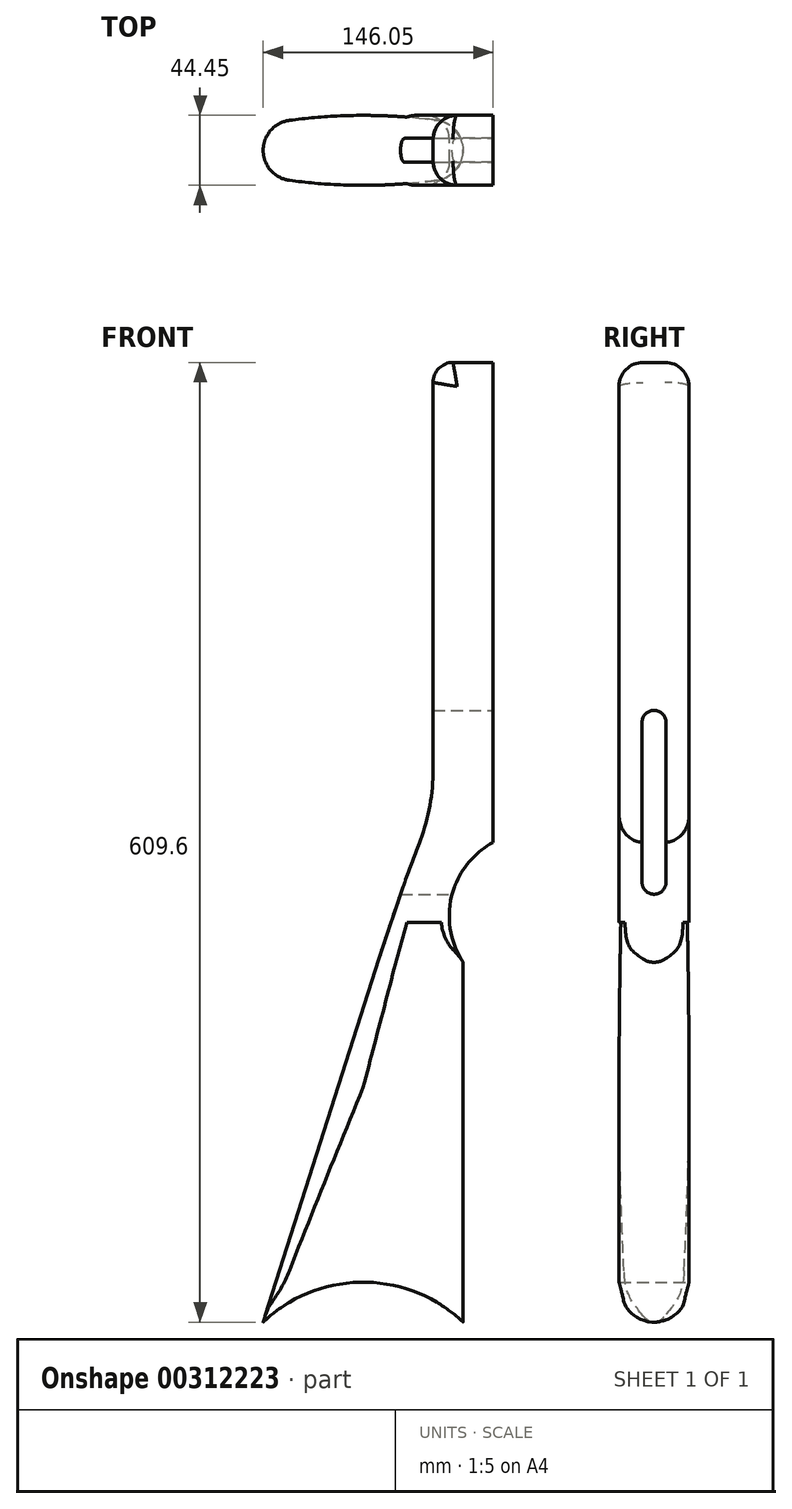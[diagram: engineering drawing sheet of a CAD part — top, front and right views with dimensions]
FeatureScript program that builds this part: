
annotation { "Feature Type Name" : "Feature", "Feature Type Description" : "" }
export const myFeature = defineFeature(function(context is Context, id is Id, definition is map)
    precondition{}
    {
        {
            var Q0;
            Q0=qCreatedBy(makeId("Front.planeOp"),FACE);
            var sketch = newSketch(context, id + "F0", { "sketchPlane" : qUnion([Q0])});
            skLineSegment(sketch, "E0.direction1", {"start": v(-1434.24, 1401.08) * mm, "end": v(-1408.84, 1401.08) * mm, "construction": true});
            skLineSegment(sketch, "E0.direction2", {"start": v(-1434.24, 1401.08) * mm, "end": v(-1434.24, 588.28) * mm, "construction": true});
            skLineSegment(sketch, "E1.1.0", {"start": v(69.19, 165.93) * mm, "end": v(69.19, -79.99) * mm});
            skArc(sketch, "E1.1.2", {"start": v(61, -124.82) * mm, "mid": v(47.45, -162.22) * mm, "end": v(34.87, -199.97) * mm});
            skLineSegment(sketch, "E1.1.3", {"start": v(34.87, -199.97) * mm, "end": v(-28, -397.22) * mm});
            skArc(sketch, "E1.1.4", {"start": v(107.29, -126.17) * mm, "mid": v(81.03, -160.1) * mm, "end": v(88.24, -202.37) * mm});
            skArc(sketch, "E1.1.5", {"start": v(69.19, -79.99) * mm, "mid": v(67.12, -102.77) * mm, "end": v(61, -124.82) * mm});
            skLineSegment(sketch, "E1.1.6", {"start": v(107.29, 178.63) * mm, "end": v(107.29, -126.17) * mm});
            skArc(sketch, "E1.1.9", {"start": v(88.24, -430.97) * mm, "mid": v(41.34, -407.08) * mm, "end": v(-10.98, -412.78) * mm});
            skLineSegment(sketch, "E1.1.11", {"start": v(88.24, -202.37) * mm, "end": v(88.24, -430.97) * mm});
            skLineSegment(sketch, "E1.1.14", {"start": v(24.74, -430.97) * mm, "end": v(24.74, -405.57) * mm, "construction": true});
            skArc(sketch, "E1.1.15", {"start": v(-28, -397.22) * mm, "mid": v(-24.47, -410.45) * mm, "end": v(-10.98, -412.78) * mm, "construction": true});
            skLineSegment(sketch, "E1.1.16", {"start": v(107.29, 178.63) * mm, "end": v(81.89, 178.63) * mm});
            skArc(sketch, "E1.1.17", {"start": v(-10.98, -412.78) * mm, "mid": v(-25.7, -420.61) * mm, "end": v(-38.76, -430.97) * mm});
            skArc(sketch, "E1.1.18", {"start": v(81.89, 178.63) * mm, "mid": v(72.9, 174.9) * mm, "end": v(69.19, 165.93) * mm});
            skLineSegment(sketch, "E2.direction1", {"start": v(107.29, -126.17) * mm, "end": v(116.81, -126.17) * mm, "construction": true});
            skLineSegment(sketch, "E3", {"start": v(-28, -397.22) * mm, "end": v(-38.76, -430.97) * mm});
            skSolve(sketch);
        }
        {
            var Q0;
            Q0=qSketchRegion(id+"F0",true);
            extrude(context, id + "F1", {"entities" : qUnion([Q0]), "depth" : 44.45 * mm});
        }
        {
            var Q0;
            Q0=makeQuery(id+"F1.opExtrude","SWEPT_FACE",FACE,{"disambiguationData":[OSD([sQuery(id+"F0.wireOp",EDGE,"E1.1.16")])]});
            var sketch = newSketch(context, id + "F2", { "sketchPlane" : qUnion([Q0])});
            skLineSegment(sketch, "E4", {"start": v(66.65, 0) * mm, "end": v(66.65, -44.95) * mm});
            skPoint(sketch, "E4.startSnap0", {"position": v(94.59, 0) * mm});
            skLineSegment(sketch, "E5", {"start": v(66.65, 0) * mm, "end": v(91.41, 0) * mm});
            skArc(sketch, "E6", {"start": v(91.41, 0) * mm, "mid": v(75.7, -6.5) * mm, "end": v(69.19, -22.23) * mm});
            skLineSegment(sketch, "E7", {"start": v(91.41, -22.23) * mm, "end": v(69.19, -22.23) * mm, "construction": true});
            skArc(sketch, "E8.MirrorCS", {"start": v(91.41, -44.45) * mm, "mid": v(75.7, -37.94) * mm, "end": v(69.19, -22.23) * mm});
            skLineSegment(sketch, "E9.MirrorCS", {"start": v(66.65, -44.45) * mm, "end": v(91.41, -44.45) * mm});
            skSolve(sketch);
        }
        {
            var Q0;
            Q0=makeQuery(id+"F1.opExtrude","CAP_EDGE",EDGE,{"disambiguationData":[OSD([sQuery(id+"F0.wireOp",EDGE,"E1.1.2")])],"isStart":true});
            var Q1;
            Q1=makeQuery(id+"F1.opExtrude","CAP_EDGE",EDGE,{"disambiguationData":[OSD([sQuery(id+"F0.wireOp",EDGE,"E1.1.0")])],"isStart":false});
            var Q2;
            Q2=makeQuery(id+"F1.opExtrude","CAP_EDGE",EDGE,{"disambiguationData":[OSD([sQuery(id+"F0.wireOp",EDGE,"E1.1.4")])],"isStart":false});
            var Q3;
            Q3=makeQuery(id+"F1.opExtrude","CAP_EDGE",EDGE,{"disambiguationData":[OSD([sQuery(id+"F0.wireOp",EDGE,"E1.1.4")])],"isStart":true});
            fillet(context, id + "F3", {"entities" : qUnion([Q0, Q1, Q2, Q3]), "radius" : 15.24 * mm, "tangentPropagation" : true, "allowEdgeOverflow" : false});
        }
        {
            var Q0;
            Q0=makeQuery(id+"F1.opExtrude","CAP_VERTEX",VERTEX,{"disambiguationData":[OSD([sQuery(id+"F0.wireOp",EDGE,"E1.1.9"),sQuery(id+"F0.wireOp",EDGE,"E1.1.11")])],"isStart":false});
            var Q1;
            Q1=makeQuery(id+"F1.opExtrude","CAP_VERTEX",VERTEX,{"disambiguationData":[OSD([sQuery(id+"F0.wireOp",EDGE,"E1.1.9"),sQuery(id+"F0.wireOp",EDGE,"E1.1.11")])],"isStart":true});
            var Q2;
            {var subQ0=sQuery(id+"F0.wireOp",EDGE,"E3");var subQ1=sQuery(id+"F0.wireOp",EDGE,"E1.1.3");Q2=makeQuery(id+"F3.opFillet","BLEND_VERTEX",VERTEX,{"blendedFrom":[makeQuery(id+"F1.opExtrude","CAP_EDGE",EDGE,{"disambiguationData":[OSD([subQ1,subQ0])],"isStart":false}),makeQuery(id+"F1.opExtrude","SWEPT_FACE",FACE,{"disambiguationData":[OSD([subQ1,subQ0])]}),makeQuery(id+"F1.opExtrude","SWEPT_FACE",FACE,{"disambiguationData":[OSD([sQuery(id+"F0.wireOp",EDGE,"E1.1.9"),sQuery(id+"F0.wireOp",EDGE,"E1.1.17")])]})],"blendedInto":[makeQuery(id+"F1.opExtrude","SWEPT_FACE",FACE,{"disambiguationData":[OSD([subQ1,subQ0])]}),makeQuery(id+"F1.opExtrude","SWEPT_FACE",FACE,{"disambiguationData":[OSD([sQuery(id+"F0.wireOp",EDGE,"E1.1.9"),sQuery(id+"F0.wireOp",EDGE,"E1.1.17")])]})]});}
            cPlane(context, id + "F4", {"entities" : qUnion([Q0, Q1, Q2]), "cplaneType" : CPlaneType.THREE_POINT, "offset" : 25.4 * mm, "width" : 152.4 * mm, "height" : 152.4 * mm});
        }
        {
            var Q0;
            Q0=qCreatedBy(id+"F4.planeOp",FACE);
            var sketch = newSketch(context, id + "F5", { "sketchPlane" : qUnion([Q0])});
            skLineSegment(sketch, "E10", {"start": v(-38.76, 22.23) * mm, "end": v(88.24, 22.23) * mm, "construction": true});
            skArc(sketch, "E11", {"start": v(88.24, 22.22) * mm, "mid": v(83.5, 34.87) * mm, "end": v(71.6, 41.27) * mm});
            skArc(sketch, "E12", {"start": v(71.6, 41.27) * mm, "mid": v(48.22, 43.66) * mm, "end": v(24.74, 44.45) * mm});
            skLineSegment(sketch, "E13", {"start": v(24.74, 44.45) * mm, "end": v(24.74, 22.23) * mm, "construction": true});
            skLineSegment(sketch, "E14", {"start": v(88.24, 44.45) * mm, "end": v(24.74, 44.45) * mm, "construction": true});
            skLineSegment(sketch, "E15", {"start": v(88.24, 22.22) * mm, "end": v(88.24, 0) * mm, "construction": true});
            skArc(sketch, "E16.MirrorCS", {"start": v(-22.13, 41.27) * mm, "mid": v(1.25, 43.66) * mm, "end": v(24.74, 44.45) * mm});
            skArc(sketch, "E17.MirrorCS", {"start": v(-38.76, 22.22) * mm, "mid": v(-34.02, 34.87) * mm, "end": v(-22.13, 41.27) * mm});
            skArc(sketch, "E18.MirrorCS", {"start": v(88.24, 22.23) * mm, "mid": v(83.5, 9.58) * mm, "end": v(71.6, 3.18) * mm});
            skArc(sketch, "E19.MirrorCS", {"start": v(71.6, 3.18) * mm, "mid": v(48.22, 0.8) * mm, "end": v(24.74, 0) * mm});
            skArc(sketch, "E20.MirrorCS", {"start": v(-22.13, 3.18) * mm, "mid": v(1.25, 0.8) * mm, "end": v(24.74, 0) * mm});
            skArc(sketch, "E21.MirrorCS", {"start": v(-38.76, 22.23) * mm, "mid": v(-34.02, 9.58) * mm, "end": v(-22.13, 3.18) * mm});
            skLineSegment(sketch, "E22.bottom", {"start": v(100.94, -12.7) * mm, "end": v(-51.46, -12.7) * mm});
            skLineSegment(sketch, "E22.top", {"start": v(100.94, 57.15) * mm, "end": v(-51.46, 57.15) * mm});
            skLineSegment(sketch, "E22.left", {"start": v(100.94, -12.7) * mm, "end": v(100.94, 57.15) * mm});
            skLineSegment(sketch, "E22.right", {"start": v(-51.46, -12.7) * mm, "end": v(-51.46, 57.15) * mm});
            skPoint(sketch, "E22.middle", {"position": v(24.74, 22.23) * mm});
            skSolve(sketch);
        }
        {
            var Q0;
            Q0=qSketchRegion(id+"F5",true);
            extrude(context, id + "F6", {"entities" : qUnion([Q0]), "operationType" : NewBodyOperationType.REMOVE, "oppositeDirection" : true, "depth" : 254 * mm});
        }
        {
            var Q0;
            Q0=makeQuery(id+"F1.opExtrude","SWEPT_FACE",FACE,{"disambiguationData":[OSD([sQuery(id+"F0.wireOp",EDGE,"E1.1.6")])]});
            var sketch = newSketch(context, id + "F7", { "sketchPlane" : qUnion([Q0])});
            skLineSegment(sketch, "E23", {"start": v(-22.23, 178.63) * mm, "end": v(-22.23, -431.6) * mm, "construction": true});
            skLineSegment(sketch, "E24.bottom", {"start": v(-14.6, -151.57) * mm, "end": v(-29.84, -151.57) * mm, "construction": true});
            skLineSegment(sketch, "E24.top", {"start": v(-22.22, -49.97) * mm, "end": v(-29.84, -49.97) * mm, "construction": true});
            skLineSegment(sketch, "E24.left", {"start": v(-14.6, -151.57) * mm, "end": v(-14.6, -49.97) * mm});
            skLineSegment(sketch, "E24.right", {"start": v(-29.84, -151.57) * mm, "end": v(-29.84, -49.97) * mm});
            skPoint(sketch, "E24.middle", {"position": v(-22.22, -100.77) * mm});
            skArc(sketch, "E25", {"start": v(-14.6, -49.97) * mm, "mid": v(-22.22, -42.35) * mm, "end": v(-29.84, -49.97) * mm});
            skArc(sketch, "E26", {"start": v(-29.84, -151.57) * mm, "mid": v(-22.22, -159.2) * mm, "end": v(-14.6, -151.57) * mm});
            skSolve(sketch);
        }
        {
            var Q0;
            Q0=qSketchRegion(id+"F7",true);
            extrude(context, id + "F8", {"entities" : qUnion([Q0]), "operationType" : NewBodyOperationType.REMOVE, "endBound" : BoundingType.THROUGH_ALL, "oppositeDirection" : true, "depth" : 25.4 * mm});
        }
    });
